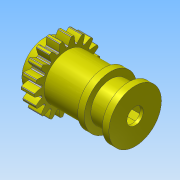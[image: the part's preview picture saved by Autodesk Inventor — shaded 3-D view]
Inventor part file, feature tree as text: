
AUTODESK INVENTOR PART (.ipt)
format: ipt  version: 2015 (Build 190159000, 159)  size: 397,312 bytes
history: native  units: mm
features: other x3, fillet x1
ambient origin geometry x8: Origin, YZ Plane, XZ Plane, XY Plane, X Axis, Y Axis, Z Axis, Center Point
bodies: Volumenkörper1 (feature_tree)
feature tree (4):
  other  "Welle_V4.iam"
  other  "Welle:1::Welle:1"
  other  "Zahnrad.iam:1::Stirnräder:1::Stirnzahnrad1:1"
  fillet  "Rundung1"  Radius=10.0mm
